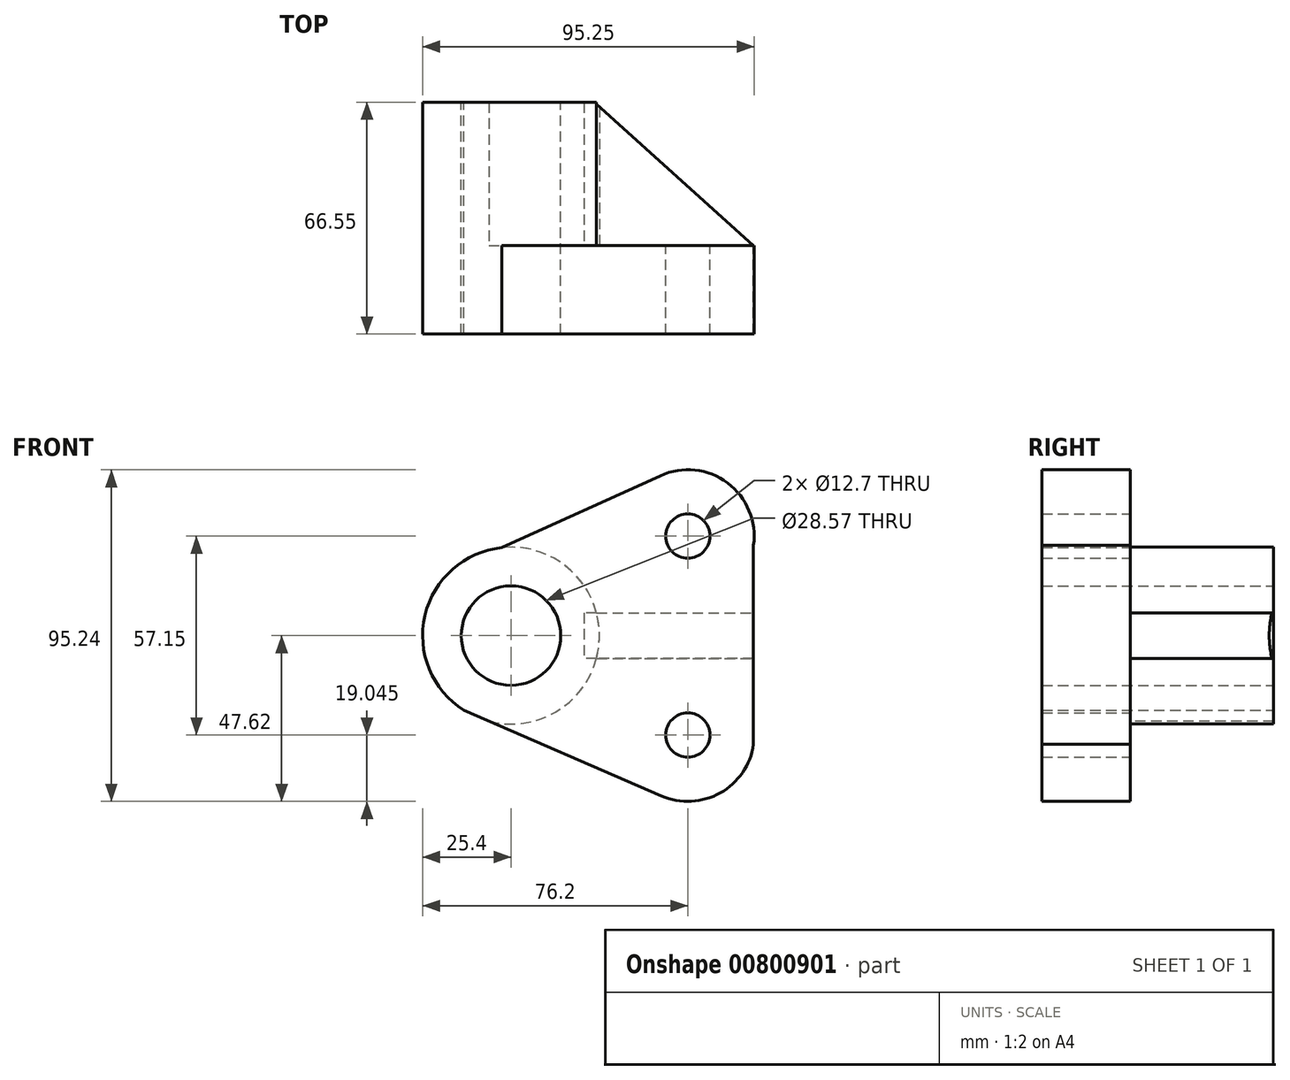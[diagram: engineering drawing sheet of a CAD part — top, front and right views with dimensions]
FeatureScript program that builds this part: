
annotation { "Feature Type Name" : "Feature", "Feature Type Description" : "" }
export const myFeature = defineFeature(function(context is Context, id is Id, definition is map)
    precondition{}
    {
        {
            var Q0;
            Q0=qCreatedBy(makeId("Front.planeOp"),FACE);
            var sketch = newSketch(context, id + "F0", { "sketchPlane" : qUnion([Q0])});
            skCircle(sketch, "E0", {"center": v(-20.94, 0) * mm, "radius": 14.29 * mm});
            skArc(sketch, "E1", {"start": v(-27.32, -24.59) * mm, "mid": v(-10.85, 23.31) * mm, "end": v(-34.5, -21.48) * mm});
            skLineSegment(sketch, "E2", {"start": v(-20.94, 0) * mm, "end": v(29.86, 0) * mm});
            skLineSegment(sketch, "E3", {"start": v(29.86, -22.23) * mm, "end": v(29.86, -28.58) * mm});
            skLineSegment(sketch, "E4", {"start": v(29.86, 22.23) * mm, "end": v(29.86, 28.58) * mm});
            skCircle(sketch, "E5", {"center": v(29.86, -28.58) * mm, "radius": 6.35 * mm});
            skArc(sketch, "E6", {"start": v(22.3, -46.06) * mm, "mid": v(41.41, -43.72) * mm, "end": v(48.72, -25.9) * mm});
            skCircle(sketch, "E7", {"center": v(29.86, 28.58) * mm, "radius": 6.35 * mm});
            skArc(sketch, "E8", {"start": v(48.72, 25.9) * mm, "mid": v(41.28, 43.82) * mm, "end": v(22, 45.93) * mm});
            skLineSegment(sketch, "E9", {"start": v(-34.5, -21.48) * mm, "end": v(22.3, -46.06) * mm});
            skLineSegment(sketch, "E10", {"start": v(48.72, 25.9) * mm, "end": v(48.72, -31.24) * mm});
            skLineSegment(sketch, "E11", {"start": v(-23.59, 25.26) * mm, "end": v(22, 45.93) * mm});
            skLineSegment(sketch, "E12", {"start": v(4.46, 0) * mm, "end": v(48.72, 0) * mm});
            skLineSegment(sketch, "E13.bottom", {"start": v(48.72, 6.48) * mm, "end": v(0, 6.48) * mm});
            skLineSegment(sketch, "E13.top", {"start": v(48.72, -6.58) * mm, "end": v(0, -6.58) * mm});
            skLineSegment(sketch, "E13.left", {"start": v(48.72, 6.48) * mm, "end": v(48.72, -6.58) * mm});
            skLineSegment(sketch, "E13.right", {"start": v(0, 6.48) * mm, "end": v(0, -6.58) * mm});
            skSolve(sketch);
        }
        {
            var Q0;
            Q0=makeQuery(id+"F0.imprint","IMPRINT",FACE,{"disambiguationData":[TD([[makeQuery(id+"F0.imprint","IMPRINT",EDGE,{"derivedFrom":sQuery(id+"F0.wireOp",EDGE,"E5")}),-1.0]])]});
            var Q1;
            Q1=makeQuery(id+"F0.imprint","IMPRINT",FACE,{"disambiguationData":[TD([[makeQuery(id+"F0.imprint","IMPRINT",EDGE,{"derivedFrom":sQuery(id+"F0.wireOp",EDGE,"E0")}),-1.0]])]});
            var Q2;
            Q2=makeQuery(id+"F0.imprint","IMPRINT",FACE,{"disambiguationData":[TD([[makeQuery(id+"F0.imprint","IMPRINT",EDGE,{"derivedFrom":sQuery(id+"F0.wireOp",EDGE,"E7")}),-1.0]])]});
            var Q3;
            {var subQ5=sQuery(id+"F0.wireOp",EDGE,"E12");var subQ7=makeQuery(id+"F0.imprint","IMPRINT",VERTEX,{"derivedFrom":subQ5});Q3=makeQuery(id+"F0.imprint","IMPRINT",FACE,{"disambiguationData":[TD([[makeQuery(id+"F0.imprint","IMPRINT",EDGE,{"disambiguationData":[TD([[subQ7,-1.0]])],"derivedFrom":subQ5}),1.0]])]});}
            var Q4;
            {var subQ1=sQuery(id+"F0.wireOp",EDGE,"E12");var subQ3=makeQuery(id+"F0.imprint","IMPRINT",VERTEX,{"derivedFrom":subQ1});Q4=makeQuery(id+"F0.imprint","IMPRINT",FACE,{"disambiguationData":[TD([[makeQuery(id+"F0.imprint","IMPRINT",EDGE,{"disambiguationData":[TD([[subQ3,-1.0]])],"derivedFrom":subQ1}),-1.0]])]});}
            var Q5;
            {var subQ3=sQuery(id+"F0.wireOp",EDGE,"E13.bottom");var subQ5=sQuery(id+"F0.wireOp",EDGE,"E13.right");var subQ7=makeQuery(id+"F0.imprint","INTERSECT",VERTEX,{"derivedFrom":[subQ3,subQ5]});Q5=makeQuery(id+"F0.imprint","IMPRINT",FACE,{"disambiguationData":[TD([[makeQuery(id+"F0.imprint","IMPRINT",EDGE,{"disambiguationData":[TD([[subQ7,1.0]])],"derivedFrom":subQ3}),1.0]])]});}
            var Q6;
            {var subQ3=sQuery(id+"F0.wireOp",EDGE,"E13.top");var subQ5=sQuery(id+"F0.wireOp",EDGE,"E13.right");var subQ6=makeQuery(id+"F0.imprint","INTERSECT",VERTEX,{"derivedFrom":[subQ3,subQ5]});Q6=makeQuery(id+"F0.imprint","IMPRINT",FACE,{"disambiguationData":[TD([[makeQuery(id+"F0.imprint","IMPRINT",EDGE,{"disambiguationData":[TD([[subQ6,1.0]])],"derivedFrom":subQ3}),-1.0]])]});}
            extrude(context, id + "F1", {"entities" : qUnion([Q0, Q1, Q2, Q3, Q4, Q5, Q6]), "depth" : 25.4 * mm, "offsetDistance" : 25.4 * mm});
        }
        {
            var Q0;
            Q0=makeQuery(id+"F0.imprint","IMPRINT",FACE,{"disambiguationData":[TD([[makeQuery(id+"F0.imprint","IMPRINT",EDGE,{"derivedFrom":sQuery(id+"F0.wireOp",EDGE,"E0")}),-1.0]])]});
            extrude(context, id + "F2", {"entities" : qUnion([Q0]), "operationType" : NewBodyOperationType.ADD, "oppositeDirection" : true, "depth" : 41.15 * mm, "offsetDistance" : 25.4 * mm});
        }
        {
            var Q0;
            {var subQ1=sQuery(id+"F0.wireOp",EDGE,"E12");var subQ3=makeQuery(id+"F0.imprint","IMPRINT",VERTEX,{"derivedFrom":subQ1});Q0=makeQuery(id+"F0.imprint","IMPRINT",FACE,{"disambiguationData":[TD([[makeQuery(id+"F0.imprint","IMPRINT",EDGE,{"disambiguationData":[TD([[subQ3,-1.0]])],"derivedFrom":subQ1}),-1.0]])]});}
            var Q1;
            {var subQ5=sQuery(id+"F0.wireOp",EDGE,"E12");var subQ7=makeQuery(id+"F0.imprint","IMPRINT",VERTEX,{"derivedFrom":subQ5});Q1=makeQuery(id+"F0.imprint","IMPRINT",FACE,{"disambiguationData":[TD([[makeQuery(id+"F0.imprint","IMPRINT",EDGE,{"disambiguationData":[TD([[subQ7,-1.0]])],"derivedFrom":subQ5}),1.0]])]});}
            extrude(context, id + "F3", {"entities" : qUnion([Q0, Q1]), "oppositeDirection" : true, "depth" : 40.64 * mm, "offsetDistance" : 25.4 * mm});
        }
        {
            var Q0;
            Q0=makeQuery(id+"F3.opExtrude","SWEPT_FACE",FACE,{"disambiguationData":[OSD([sQuery(id+"F0.wireOp",EDGE,"E13.bottom")])]});
            var sketch = newSketch(context, id + "F4", { "sketchPlane" : qUnion([Q0])});
            skLineSegment(sketch, "E14", {"start": v(3.62, 40.64) * mm, "end": v(48.72, 0) * mm});
            skSolve(sketch);
        }
        {
            var Q0;
            Q0=makeQuery(id+"F4.imprint","IMPRINT",FACE,{"disambiguationData":[TD([[makeQuery(id+"F4.imprint","IMPRINT",EDGE,{"derivedFrom":sQuery(id+"F4.wireOp",EDGE,"E14")}),1.0]])]});
            extrude(context, id + "F5", {"entities" : qUnion([Q0]), "operationType" : NewBodyOperationType.REMOVE, "oppositeDirection" : true, "depth" : 25.4 * mm, "offsetDistance" : 25.4 * mm});
        }
    });
